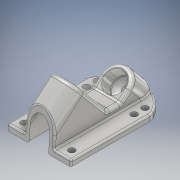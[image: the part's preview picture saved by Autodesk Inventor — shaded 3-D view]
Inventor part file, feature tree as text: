
AUTODESK INVENTOR PART (.ipt)
format: ipt  version: 2019 (Build 230136000, 136)  size: 448,000 bytes
history: native  units: mm
features: sketch x10, extrude x9, other x6, fillet x5, projected_geometry x4, revolve x1
ambient origin geometry x8: Origin, YZ Plane, XZ Plane, XY Plane, X Axis, Y Axis, Z Axis, Center Point
bodies: Body1 (feature_tree)
feature tree (35):
  other  "Твердое тело1"
  extrude  "Выдавливание1"  Depth=55.6mm
  other  "РабПлоскость1"
  extrude  "Выдавливание2"  Depth=88.5mm
  extrude  "Выдавливание3"  Depth=54.0mm
  fillet  "Сопряжение1"  Radius=63.5mm
  extrude  "Выдавливание4"  Depth=41.3mm
  other  "РабПлоскость3"
  other  "НаклГрань1"
  extrude  "Выдавливание5"  Depth=5.5mm
  extrude  "Выдавливание6"  Depth=5.0mm TaperAngle=0.0deg
  extrude  "Выдавливание7"  Depth=8.726646mm
  extrude  "Выдавливание8"  Depth=6.0mm
  fillet  "Сопряжение2"  Radius=25.0mm
  fillet  "Сопряжение3"  Radius=25.0mm
  fillet  "Сопряжение4"  Radius=12.5mm
  other  "РабПлоскость4"
  revolve  "Вращение1"
  extrude  "Выдавливание9"  Depth=18.0mm
  fillet  "Сопряжение7"  Radius=15.0mm
  sketch  "Эскиз1"
  sketch  "Эскиз2"
  sketch  "Эскиз3"
  sketch  "Эскиз4"
  projected_geometry  "Спроецированная петля1"
  sketch  "Эскиз5"
  projected_geometry  "Спроецированная петля2"
  sketch  "Эскиз6"
  sketch  "Эскиз7"
  projected_geometry  "Спроецированная петля3"
  sketch  "Эскиз8"
  projected_geometry  "Спроецированная петля4"
  other  "РабОсь1"
  sketch  "Эскиз9"
  sketch  "Эскиз10"
